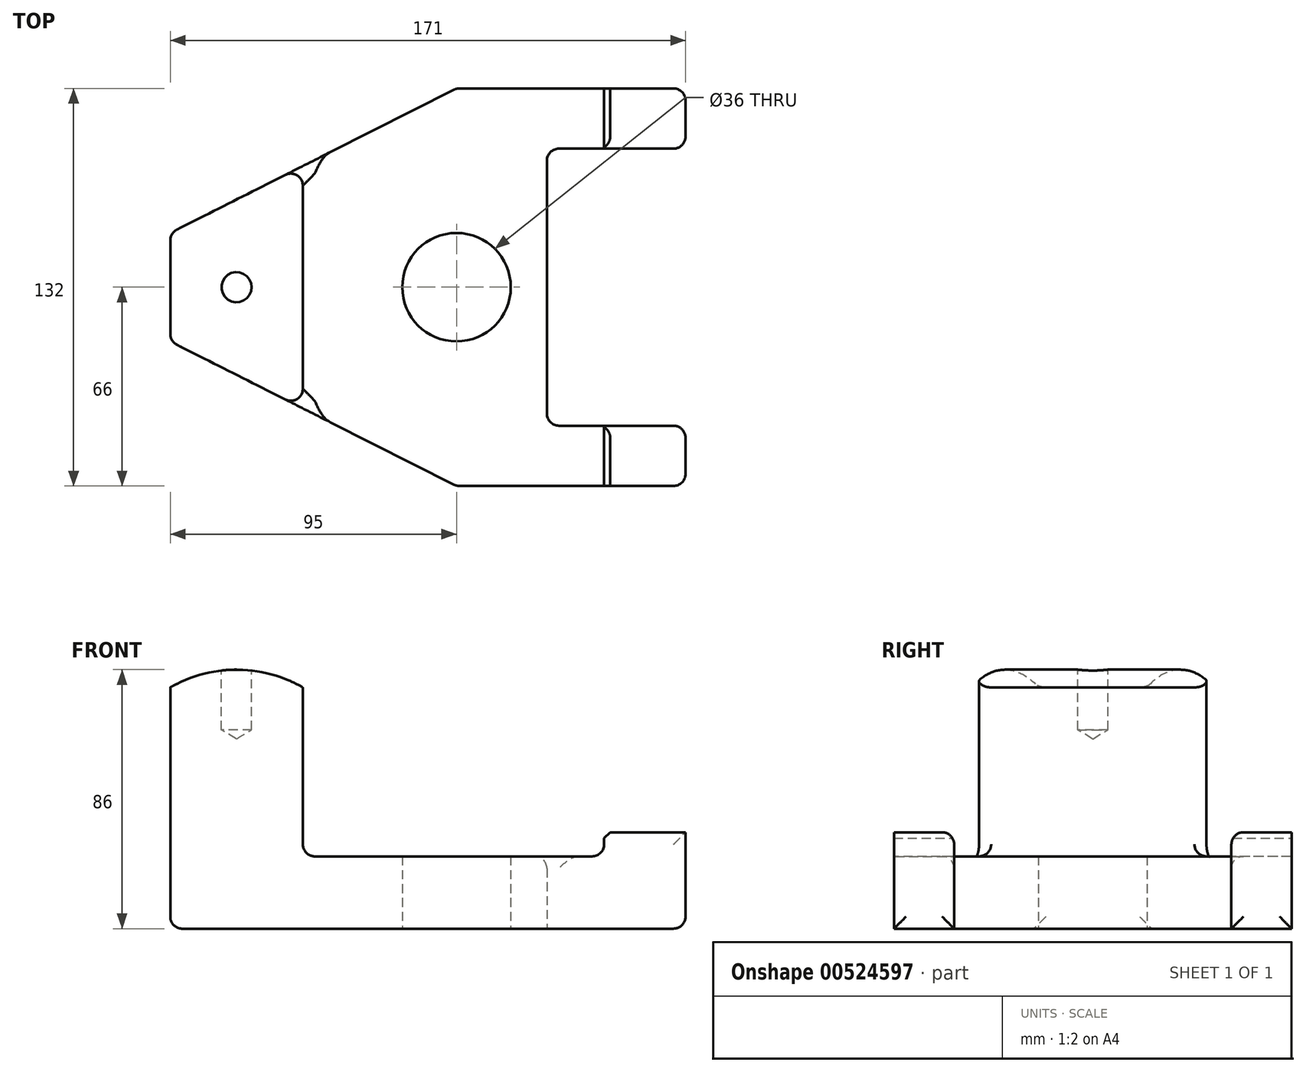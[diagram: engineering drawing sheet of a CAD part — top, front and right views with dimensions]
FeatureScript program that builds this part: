
annotation { "Feature Type Name" : "Feature", "Feature Type Description" : "" }
export const myFeature = defineFeature(function(context is Context, id is Id, definition is map)
    precondition{}
    {
        {
            var Q0;
            Q0=qCreatedBy(makeId("Top.planeOp"),FACE);
            var sketch = newSketch(context, id + "F0", { "sketchPlane" : qUnion([Q0])});
            skLineSegment(sketch, "E0", {"start": v(-115.36, 0) * mm, "end": v(123.75, 0) * mm, "construction": true});
            skCircle(sketch, "E1", {"center": v(0, 0) * mm, "radius": 18 * mm});
            skLineSegment(sketch, "E2", {"start": v(-95, 18) * mm, "end": v(-95, 0) * mm});
            skLineSegment(sketch, "E3", {"start": v(-95, 0) * mm, "end": v(30, 0) * mm});
            skLineSegment(sketch, "E4", {"start": v(30, 0) * mm, "end": v(30, 46) * mm});
            skLineSegment(sketch, "E5", {"start": v(30, 46) * mm, "end": v(76, 46) * mm});
            skLineSegment(sketch, "E6", {"start": v(76, 46) * mm, "end": v(76, 66) * mm});
            skLineSegment(sketch, "E7", {"start": v(76, 66) * mm, "end": v(0, 66) * mm});
            skLineSegment(sketch, "E8", {"start": v(0, 66) * mm, "end": v(-95, 18) * mm});
            skLineSegment(sketch, "E9.MirrorCS", {"start": v(-95, -18) * mm, "end": v(-95, 0) * mm});
            skLineSegment(sketch, "E10.MirrorCS", {"start": v(0, -66) * mm, "end": v(-95, -18) * mm});
            skLineSegment(sketch, "E11.MirrorCS", {"start": v(30, 0) * mm, "end": v(30, -46) * mm});
            skLineSegment(sketch, "E12.MirrorCS", {"start": v(30, -46) * mm, "end": v(76, -46) * mm});
            skLineSegment(sketch, "E13.MirrorCS", {"start": v(76, -46) * mm, "end": v(76, -66) * mm});
            skLineSegment(sketch, "E14.MirrorCS", {"start": v(76, -66) * mm, "end": v(0, -66) * mm});
            skSolve(sketch);
        }
        {
            var Q0;
            Q0 = qSketchRegion(id + "F0", true);
            extrude(context, id + "F1", {"entities" : qUnion([Q0]), "depth" : 86 * mm, "offsetDistance" : 25 * mm});
        }
        {
            var Q0;
            Q0=qCreatedBy(makeId("Front.planeOp"),FACE);
            var sketch = newSketch(context, id + "F2", { "sketchPlane" : qUnion([Q0])});
            skLineSegment(sketch, "E15.0", {"start": v(-95, 86) * mm, "end": v(-95, 0) * mm});
            skLineSegment(sketch, "E16.0", {"start": v(0, 0) * mm, "end": v(-95, 0) * mm});
            skLineSegment(sketch, "E17.0", {"start": v(76, 0) * mm, "end": v(0, 0) * mm});
            skLineSegment(sketch, "E18", {"start": v(76, 0) * mm, "end": v(76, 32) * mm});
            skLineSegment(sketch, "E19", {"start": v(76, 32) * mm, "end": v(49, 32) * mm});
            skLineSegment(sketch, "E20", {"start": v(49, 32) * mm, "end": v(49, 24) * mm});
            skLineSegment(sketch, "E21", {"start": v(49, 24) * mm, "end": v(-51, 24) * mm});
            skLineSegment(sketch, "E22", {"start": v(-95, 86) * mm, "end": v(-51, 86) * mm});
            skLineSegment(sketch, "E23", {"start": v(-51, 86) * mm, "end": v(-51, 24) * mm});
            skArc(sketch, "E24", {"start": v(-51, 80.1) * mm, "mid": v(-73, 86) * mm, "end": v(-95, 80.1) * mm});
            skPoint(sketch, "E24.centerSnap0", {"position": v(-73, 86) * mm});
            skLineSegment(sketch, "E25.0", {"start": v(0, 86) * mm, "end": v(-95, 86) * mm});
            skLineSegment(sketch, "E26.0", {"start": v(76, 86) * mm, "end": v(0, 86) * mm});
            skLineSegment(sketch, "E27.0", {"start": v(76, 86) * mm, "end": v(76, 0) * mm});
            skSolve(sketch);
        }
        {
            var Q0;
            {var subQ5=sQuery(id+"F2.wireOp",EDGE,"E19");Q0=makeQuery(id+"F2.imprint","IMPRINT",FACE,{"disambiguationData":[TD([[makeQuery(id+"F2.imprint","IMPRINT",EDGE,{"derivedFrom":subQ5}),-1.0]])]});}
            var Q1;
            {var subQ0=sQuery(id+"F2.wireOp",EDGE,"E25.0");var subQ1=sQuery(id+"F2.wireOp",EDGE,"E23");var subQ2=makeQuery(id+"F2.imprint","INTERSECT",VERTEX,{"derivedFrom":[subQ1,subQ0]});Q1=makeQuery(id+"F2.imprint","IMPRINT",FACE,{"disambiguationData":[TD([[makeQuery(id+"F2.imprint","IMPRINT",EDGE,{"disambiguationData":[TD([[subQ2,-1.0]])],"derivedFrom":subQ1}),-1.0]])]});}
            var Q2;
            {var subQ0=sQuery(id+"F2.wireOp",EDGE,"E25.0");var subQ1=sQuery(id+"F2.wireOp",EDGE,"E15.0");var subQ2=makeQuery(id+"F2.imprint","INTERSECT",VERTEX,{"derivedFrom":[subQ1,subQ0]});Q2=makeQuery(id+"F2.imprint","IMPRINT",FACE,{"disambiguationData":[TD([[makeQuery(id+"F2.imprint","IMPRINT",EDGE,{"disambiguationData":[TD([[subQ2,-1.0]])],"derivedFrom":subQ1}),1.0]])]});}
            extrude(context, id + "F3", {"entities" : qUnion([Q0, Q1, Q2]), "operationType" : NewBodyOperationType.REMOVE, "oppositeDirection" : true, "depth" : 132 * mm, "offsetDistance" : 25 * mm, "symmetric" : true});
        }
        {
            var Q0;
            Q0=qCreatedBy(makeId("Top.planeOp"),FACE);
            cPlane(context, id + "F4", {"entities" : qUnion([Q0]), "cplaneType" : CPlaneType.OFFSET, "offset" : 86 * mm, "width" : 150 * mm, "height" : 150 * mm});
        }
        {
            var Q0;
            Q0=qCreatedBy(id+"F4.planeOp",FACE);
            var sketch = newSketch(context, id + "F5", { "sketchPlane" : qUnion([Q0])});
            skPoint(sketch, "E28", {"position": v(-73, 0) * mm});
            skSolve(sketch);
        }
        {
            var Q0;
            Q0=sQuery(id+"F5.wireOp",VERTEX,"E28");
            var Q1;
            Q1=makeQuery(id+"F1.opExtrude","SWEPT_BODY",BODY,{"disambiguationData":[OSD([sQuery(id+"F0.wireOp",EDGE,"E2"),sQuery(id+"F0.wireOp",EDGE,"E4"),sQuery(id+"F0.wireOp",EDGE,"E5"),sQuery(id+"F0.wireOp",EDGE,"E6"),sQuery(id+"F0.wireOp",EDGE,"E7"),sQuery(id+"F0.wireOp",EDGE,"E8"),sQuery(id+"F0.wireOp",EDGE,"E9.MirrorCS"),sQuery(id+"F0.wireOp",EDGE,"E1"),sQuery(id+"F0.wireOp",EDGE,"E10.MirrorCS"),sQuery(id+"F0.wireOp",EDGE,"E11.MirrorCS"),sQuery(id+"F0.wireOp",EDGE,"E12.MirrorCS"),sQuery(id+"F0.wireOp",EDGE,"E13.MirrorCS"),sQuery(id+"F0.wireOp",EDGE,"E14.MirrorCS")])]});
            hole(context, id + "F6", {"style" : HoleStyle.SIMPLE, "endStyle" : HoleEndStyle.BLIND, "holeDiameter" : 10 * mm, "holeDepth" : 20 * mm, "tappedDepth" : 12 * mm, "tapClearance" : 3, "startFromSketch" : true, "locations" : qUnion([Q0]), "scope" : qUnion([Q1])});
        }
        {
            var Q0;
            {var subQ0=sQuery(id+"F2.wireOp",EDGE,"E19");var subQ1=sQuery(id+"F2.wireOp",EDGE,"E20");Q0=makeQuery(id+"F3.boolean.opBoolean","COPY",EDGE,{"disambiguationData":[TD([makeQuery(id+"F1.opExtrude","SWEPT_FACE",FACE,{"disambiguationData":[OSD([sQuery(id+"F0.wireOp",EDGE,"E12.MirrorCS")])]})])],"derivedFrom":makeQuery(id+"F3.opExtrude","SWEPT_EDGE",EDGE,{"disambiguationData":[OSD([subQ0,subQ1])]})});}
            var Q1;
            {var subQ0=sQuery(id+"F2.wireOp",EDGE,"E20");var subQ1=sQuery(id+"F2.wireOp",EDGE,"E19");Q1=makeQuery(id+"F3.boolean.opBoolean","COPY",EDGE,{"disambiguationData":[TD([makeQuery(id+"F1.opExtrude","SWEPT_FACE",FACE,{"disambiguationData":[OSD([sQuery(id+"F0.wireOp",EDGE,"E5")])]})])],"derivedFrom":makeQuery(id+"F3.opExtrude","SWEPT_EDGE",EDGE,{"disambiguationData":[OSD([subQ1,subQ0])]})});}
            var Q2;
            {var subQ0=sQuery(id+"F2.wireOp",EDGE,"E19");Q2=makeQuery(id+"F3.boolean.opBoolean","COPY",EDGE,{"disambiguationData":[topologyDisambiguationEdgeConnected([makeQuery(id+"F1.opExtrude","SWEPT_FACE",FACE,{"disambiguationData":[OSD([sQuery(id+"F0.wireOp",EDGE,"E6")])]})])],"derivedFrom":makeQuery(id+"F3.opExtrude","SWEPT_EDGE",EDGE,{"disambiguationData":[OSD([subQ0,sQuery(id+"F2.wireOp",EDGE,"E27.0")])]})});}
            var Q3;
            {var subQ0=sQuery(id+"F2.wireOp",EDGE,"E19");Q3=makeQuery(id+"F3.boolean.opBoolean","COPY",EDGE,{"disambiguationData":[topologyDisambiguationEdgeConnected([makeQuery(id+"F1.opExtrude","SWEPT_FACE",FACE,{"disambiguationData":[OSD([sQuery(id+"F0.wireOp",EDGE,"E13.MirrorCS")])]})])],"derivedFrom":makeQuery(id+"F3.opExtrude","SWEPT_EDGE",EDGE,{"disambiguationData":[OSD([subQ0,sQuery(id+"F2.wireOp",EDGE,"E27.0")])]})});}
            chamfer(context, id + "F7", {"entities" : qUnion([Q0, Q1, Q2, Q3]), "width" : 2 * mm, "tangentPropagation" : true});
        }
        {
            var Q0;
            Q0=makeQuery(id+"F1.opExtrude","CAP_EDGE",EDGE,{"disambiguationData":[OSD([sQuery(id+"F0.wireOp",EDGE,"E2"),sQuery(id+"F0.wireOp",EDGE,"E9.MirrorCS")])],"isStart":true});
            var Q1;
            Q1=makeQuery(id+"F1.opExtrude","SWEPT_EDGE",EDGE,{"disambiguationData":[OSD([sQuery(id+"F0.wireOp",EDGE,"E9.MirrorCS"),sQuery(id+"F0.wireOp",EDGE,"E10.MirrorCS")])]});
            var Q2;
            Q2=makeQuery(id+"F1.opExtrude","SWEPT_EDGE",EDGE,{"disambiguationData":[OSD([sQuery(id+"F0.wireOp",EDGE,"E2"),sQuery(id+"F0.wireOp",EDGE,"E8")])]});
            var Q3;
            Q3=makeQuery(id+"F1.opExtrude","SWEPT_EDGE",EDGE,{"disambiguationData":[OSD([sQuery(id+"F0.wireOp",EDGE,"E10.MirrorCS"),sQuery(id+"F0.wireOp",EDGE,"E14.MirrorCS")])]});
            var Q4;
            Q4=makeQuery(id+"F1.opExtrude","SWEPT_EDGE",EDGE,{"disambiguationData":[OSD([sQuery(id+"F0.wireOp",EDGE,"E7"),sQuery(id+"F0.wireOp",EDGE,"E8")])]});
            var Q5;
            Q5=makeQuery(id+"F1.opExtrude","SWEPT_EDGE",EDGE,{"disambiguationData":[OSD([sQuery(id+"F0.wireOp",EDGE,"E6"),sQuery(id+"F0.wireOp",EDGE,"E7")])]});
            var Q6;
            Q6=makeQuery(id+"F1.opExtrude","SWEPT_EDGE",EDGE,{"disambiguationData":[OSD([sQuery(id+"F0.wireOp",EDGE,"E5"),sQuery(id+"F0.wireOp",EDGE,"E6")])]});
            var Q7;
            Q7=makeQuery(id+"F1.opExtrude","SWEPT_EDGE",EDGE,{"disambiguationData":[OSD([sQuery(id+"F0.wireOp",EDGE,"E11.MirrorCS"),sQuery(id+"F0.wireOp",EDGE,"E12.MirrorCS")])]});
            var Q8;
            Q8=makeQuery(id+"F1.opExtrude","SWEPT_EDGE",EDGE,{"disambiguationData":[OSD([sQuery(id+"F0.wireOp",EDGE,"E4"),sQuery(id+"F0.wireOp",EDGE,"E5")])]});
            var Q9;
            Q9=makeQuery(id+"F1.opExtrude","SWEPT_EDGE",EDGE,{"disambiguationData":[OSD([sQuery(id+"F0.wireOp",EDGE,"E12.MirrorCS"),sQuery(id+"F0.wireOp",EDGE,"E13.MirrorCS")])]});
            var Q10;
            Q10=makeQuery(id+"F1.opExtrude","SWEPT_EDGE",EDGE,{"disambiguationData":[OSD([sQuery(id+"F0.wireOp",EDGE,"E13.MirrorCS"),sQuery(id+"F0.wireOp",EDGE,"E14.MirrorCS")])]});
            var Q11;
            Q11=makeQuery(id+"F1.opExtrude","CAP_EDGE",EDGE,{"disambiguationData":[OSD([sQuery(id+"F0.wireOp",EDGE,"E13.MirrorCS")])],"isStart":true});
            var Q12;
            Q12=makeQuery(id+"F1.opExtrude","CAP_EDGE",EDGE,{"disambiguationData":[OSD([sQuery(id+"F0.wireOp",EDGE,"E6")])],"isStart":true});
            var Q13;
            {var subQ0=sQuery(id+"F2.wireOp",EDGE,"E20");var subQ1=sQuery(id+"F2.wireOp",EDGE,"E21");Q13=makeQuery(id+"F3.boolean.opBoolean","COPY",EDGE,{"disambiguationData":[TD([makeQuery(id+"F1.opExtrude","SWEPT_FACE",FACE,{"disambiguationData":[OSD([sQuery(id+"F0.wireOp",EDGE,"E5")])]})])],"derivedFrom":makeQuery(id+"F3.opExtrude","SWEPT_EDGE",EDGE,{"disambiguationData":[OSD([subQ0,subQ1])]})});}
            var Q14;
            {var subQ0=sQuery(id+"F2.wireOp",EDGE,"E21");var subQ1=sQuery(id+"F2.wireOp",EDGE,"E20");Q14=makeQuery(id+"F3.boolean.opBoolean","COPY",EDGE,{"disambiguationData":[TD([makeQuery(id+"F1.opExtrude","SWEPT_FACE",FACE,{"disambiguationData":[OSD([sQuery(id+"F0.wireOp",EDGE,"E12.MirrorCS")])]})])],"derivedFrom":makeQuery(id+"F3.opExtrude","SWEPT_EDGE",EDGE,{"disambiguationData":[OSD([subQ1,subQ0])]})});}
            var Q15;
            Q15=makeQuery(id+"F3.boolean.opBoolean","COPY",EDGE,{"derivedFrom":makeQuery(id+"F3.opExtrude","SWEPT_EDGE",EDGE,{"disambiguationData":[OSD([sQuery(id+"F2.wireOp",EDGE,"E21"),sQuery(id+"F2.wireOp",EDGE,"E23")])]})});
            var Q16;
            Q16=makeQuery(id+"F3.boolean.opBoolean","INTERSECT",EDGE,{"derivedFrom":[makeQuery(id+"F1.opExtrude","SWEPT_FACE",FACE,{"disambiguationData":[OSD([sQuery(id+"F0.wireOp",EDGE,"E10.MirrorCS")])]}),makeQuery(id+"F3.opExtrude","SWEPT_FACE",FACE,{"disambiguationData":[OSD([sQuery(id+"F2.wireOp",EDGE,"E23")])]})]});
            var Q17;
            Q17=makeQuery(id+"F3.boolean.opBoolean","INTERSECT",EDGE,{"derivedFrom":[makeQuery(id+"F1.opExtrude","SWEPT_FACE",FACE,{"disambiguationData":[OSD([sQuery(id+"F0.wireOp",EDGE,"E8")])]}),makeQuery(id+"F3.opExtrude","SWEPT_FACE",FACE,{"disambiguationData":[OSD([sQuery(id+"F2.wireOp",EDGE,"E23")])]})]});
            var Q18;
            Q18=makeQuery(id+"F3.boolean.opBoolean","COPY",EDGE,{"derivedFrom":makeQuery(id+"F3.opExtrude","CAP_EDGE",EDGE,{"disambiguationData":[OSD([sQuery(id+"F2.wireOp",EDGE,"E21")])],"isStart":true})});
            var Q19;
            Q19=makeQuery(id+"F3.boolean.opBoolean","COPY",EDGE,{"derivedFrom":makeQuery(id+"F3.opExtrude","CAP_EDGE",EDGE,{"disambiguationData":[OSD([sQuery(id+"F2.wireOp",EDGE,"E21")])],"isStart":false})});
            var Q20;
            Q20=makeQuery(id+"F3.boolean.opBoolean","COPY",EDGE,{"derivedFrom":makeQuery(id+"F3.opExtrude","CAP_EDGE",EDGE,{"disambiguationData":[OSD([sQuery(id+"F2.wireOp",EDGE,"E19")])],"isStart":false})});
            var Q21;
            Q21=makeQuery(id+"F3.boolean.opBoolean","INTERSECT",EDGE,{"derivedFrom":[makeQuery(id+"F1.opExtrude","SWEPT_FACE",FACE,{"disambiguationData":[OSD([sQuery(id+"F0.wireOp",EDGE,"E5")])]}),makeQuery(id+"F3.opExtrude","SWEPT_FACE",FACE,{"disambiguationData":[OSD([sQuery(id+"F2.wireOp",EDGE,"E19")])]})]});
            var Q22;
            Q22=makeQuery(id+"F3.boolean.opBoolean","COPY",EDGE,{"derivedFrom":makeQuery(id+"F3.opExtrude","CAP_EDGE",EDGE,{"disambiguationData":[OSD([sQuery(id+"F2.wireOp",EDGE,"E19")])],"isStart":true})});
            var Q23;
            Q23=makeQuery(id+"F3.boolean.opBoolean","INTERSECT",EDGE,{"derivedFrom":[makeQuery(id+"F1.opExtrude","SWEPT_FACE",FACE,{"disambiguationData":[OSD([sQuery(id+"F0.wireOp",EDGE,"E12.MirrorCS")])]}),makeQuery(id+"F3.opExtrude","SWEPT_FACE",FACE,{"disambiguationData":[OSD([sQuery(id+"F2.wireOp",EDGE,"E19")])]})]});
            var Q24;
            Q24=makeQuery(id+"F3.boolean.opBoolean","INTERSECT",EDGE,{"derivedFrom":[makeQuery(id+"F1.opExtrude","SWEPT_FACE",FACE,{"disambiguationData":[OSD([sQuery(id+"F0.wireOp",EDGE,"E4"),sQuery(id+"F0.wireOp",EDGE,"E11.MirrorCS")])]}),makeQuery(id+"F3.opExtrude","SWEPT_FACE",FACE,{"disambiguationData":[OSD([sQuery(id+"F2.wireOp",EDGE,"E21")])]})]});
            fillet(context, id + "F8", {"entities" : qUnion([Q0, Q1, Q2, Q3, Q4, Q5, Q6, Q7, Q8, Q9, Q10, Q11, Q12, Q13, Q14, Q15, Q16, Q17, Q18, Q19, Q20, Q21, Q22, Q23, Q24]), "radius" : 4 * mm, "tangentPropagation" : true, "allowEdgeOverflow" : false});
        }
    });
